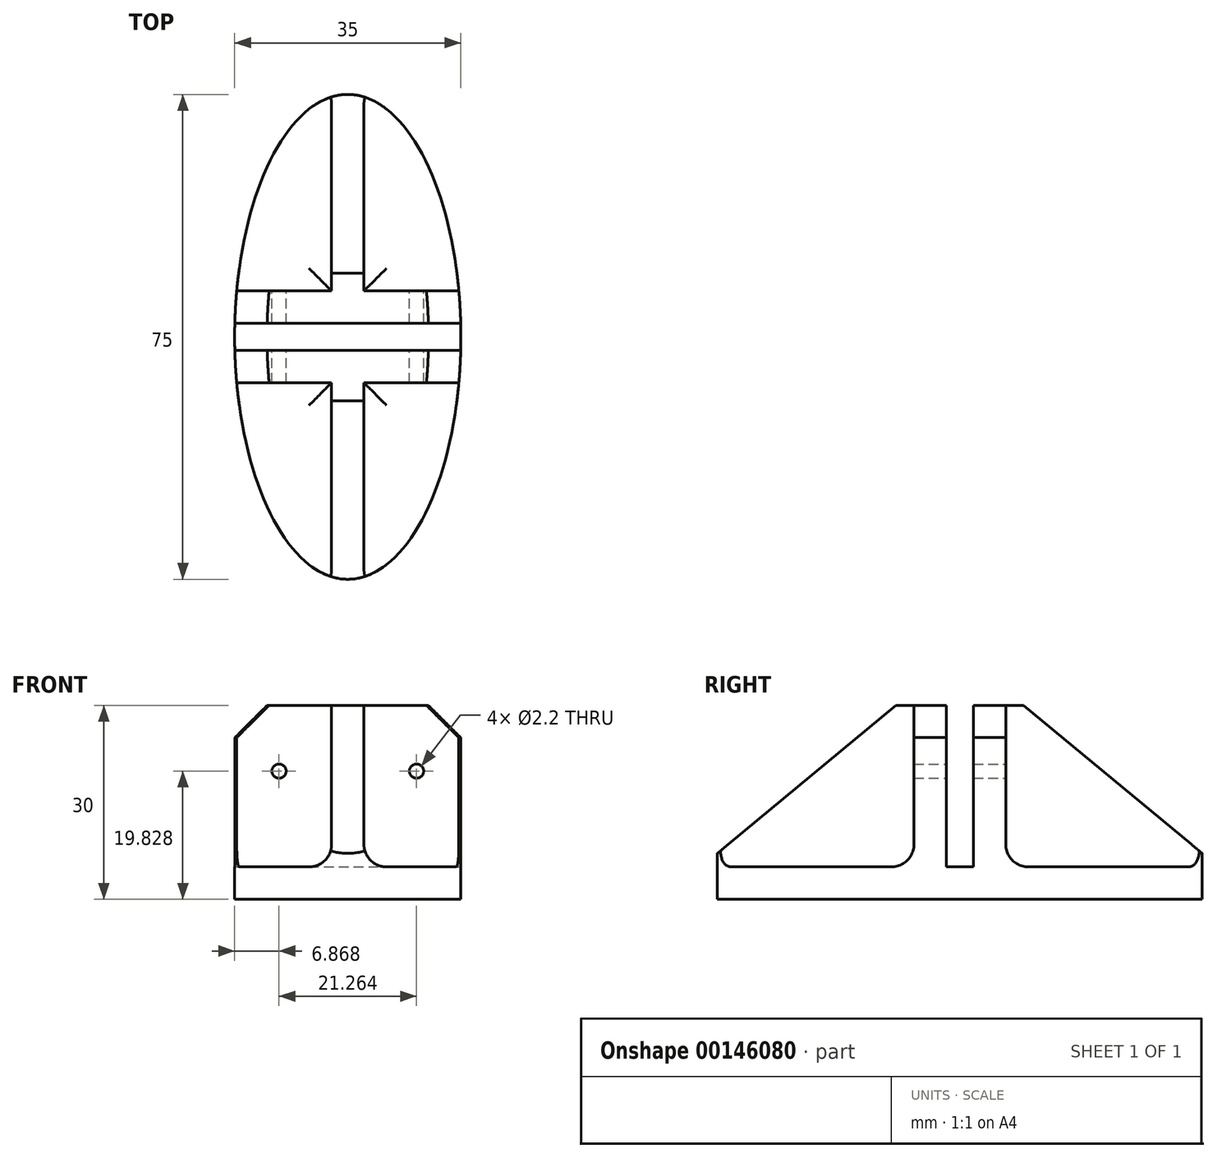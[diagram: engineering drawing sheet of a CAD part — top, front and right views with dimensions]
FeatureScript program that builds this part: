
annotation { "Feature Type Name" : "Feature", "Feature Type Description" : "" }
export const myFeature = defineFeature(function(context is Context, id is Id, definition is map)
    precondition{}
    {
        {
            var Q0;
            Q0=qCreatedBy(makeId("Top.planeOp"),FACE);
            var sketch = newSketch(context, id + "F0", { "sketchPlane" : qUnion([Q0])});
            skEllipse(sketch, "E0", {"center": v(0, 0) * mm, "majorRadius": 37.5 * mm, "minorRadius": 17.5 * mm, "majorAxis": v(0, 1)});
            skSolve(sketch);
        }
        {
            var Q0;
            Q0 = qSketchRegion(id + "F0", true);
            extrude(context, id + "F1", {"entities" : qUnion([Q0]), "depth" : 30 * mm});
        }
        {
            var Q0;
            Q0=makeQuery(id+"F1.opExtrude","CAP_FACE",FACE,{"disambiguationData":[OSD([sQuery(id+"F0.wireOp",EDGE,"E0")])],"isStart":false});
            var sketch = newSketch(context, id + "F2", { "sketchPlane" : qUnion([Q0])});
            skLineSegment(sketch, "E1.bottom", {"start": v(-21.5, 2.1) * mm, "end": v(21.5, 2.1) * mm});
            skLineSegment(sketch, "E1.top", {"start": v(-21.5, -2.1) * mm, "end": v(21.5, -2.1) * mm});
            skLineSegment(sketch, "E1.left", {"start": v(-21.5, 2.1) * mm, "end": v(-21.5, -2.1) * mm});
            skLineSegment(sketch, "E1.right", {"start": v(21.5, 2.1) * mm, "end": v(21.5, -2.1) * mm});
            skPoint(sketch, "E1.middle", {"position": v(0, 0) * mm});
            skSolve(sketch);
        }
        {
            var Q0;
            Q0 = qSketchRegion(id + "F2", true);
            extrude(context, id + "F3", {"entities" : qUnion([Q0]), "operationType" : NewBodyOperationType.REMOVE, "oppositeDirection" : true, "depth" : 25 * mm});
        }
        {
            var Q0;
            {var subQ0=sQuery(id+"F0.wireOp",EDGE,"E0");Q0=makeQuery(id+"F3.boolean.opBoolean","SPLIT",FACE,{"disambiguationData":[TD([makeQuery(id+"F3.opExtrude","SWEPT_FACE",FACE,{"disambiguationData":[OSD([sQuery(id+"F2.wireOp",EDGE,"E1.bottom")])]})])],"derivedFrom":makeQuery(id+"F1.opExtrude","CAP_FACE",FACE,{"disambiguationData":[OSD([subQ0])],"isStart":false})});}
            var sketch = newSketch(context, id + "F4", { "sketchPlane" : qUnion([Q0])});
            skLineSegment(sketch, "E2.bottom", {"start": v(-21.55, 7.1) * mm, "end": v(-2.5, 7.1) * mm});
            skLineSegment(sketch, "E2.top", {"start": v(-21.55, 47.53) * mm, "end": v(-2.5, 47.53) * mm});
            skLineSegment(sketch, "E2.left", {"start": v(-21.55, 7.1) * mm, "end": v(-21.55, 47.53) * mm});
            skLineSegment(sketch, "E2.right", {"start": v(-2.5, 7.1) * mm, "end": v(-2.5, 47.53) * mm});
            skLineSegment(sketch, "E3.MirrorCS", {"start": v(2.5, 7.1) * mm, "end": v(2.5, 47.53) * mm});
            skLineSegment(sketch, "E4.MirrorCS", {"start": v(21.55, 7.1) * mm, "end": v(21.55, 47.53) * mm});
            skLineSegment(sketch, "E5.MirrorCS", {"start": v(21.55, 7.1) * mm, "end": v(2.5, 7.1) * mm});
            skLineSegment(sketch, "E6.MirrorCS", {"start": v(21.55, 47.53) * mm, "end": v(2.5, 47.53) * mm});
            skLineSegment(sketch, "E7.MirrorCS", {"start": v(21.55, -7.1) * mm, "end": v(2.5, -7.1) * mm});
            skLineSegment(sketch, "E8.MirrorCS", {"start": v(21.55, -7.1) * mm, "end": v(21.55, -47.53) * mm});
            skLineSegment(sketch, "E9.MirrorCS", {"start": v(2.5, -7.1) * mm, "end": v(2.5, -47.53) * mm});
            skLineSegment(sketch, "E10.MirrorCS", {"start": v(-2.5, -7.1) * mm, "end": v(-2.5, -47.53) * mm});
            skLineSegment(sketch, "E11.MirrorCS", {"start": v(-21.55, -7.1) * mm, "end": v(-21.55, -47.53) * mm});
            skLineSegment(sketch, "E12.MirrorCS", {"start": v(-21.55, -47.53) * mm, "end": v(-2.5, -47.53) * mm});
            skLineSegment(sketch, "E13.MirrorCS", {"start": v(21.55, -47.53) * mm, "end": v(2.5, -47.53) * mm});
            skLineSegment(sketch, "E14.MirrorCS", {"start": v(-21.55, -7.1) * mm, "end": v(-2.5, -7.1) * mm});
            skSolve(sketch);
        }
        {
            var Q0;
            Q0 = qSketchRegion(id + "F4", true);
            extrude(context, id + "F5", {"entities" : qUnion([Q0]), "operationType" : NewBodyOperationType.REMOVE, "oppositeDirection" : true, "depth" : 25 * mm});
        }
        {
            var Q0;
            Q0=qCreatedBy(makeId("Right.planeOp"),FACE);
            var sketch = newSketch(context, id + "F6", { "sketchPlane" : qUnion([Q0])});
            skLineSegment(sketch, "E15", {"start": v(5.91, 33.28) * mm, "end": v(42.13, 3.27) * mm});
            skLineSegment(sketch, "E16", {"start": v(42.13, 3.27) * mm, "end": v(40.75, 34.27) * mm});
            skLineSegment(sketch, "E17", {"start": v(40.75, 34.27) * mm, "end": v(5.91, 33.28) * mm});
            skLineSegment(sketch, "E18.MirrorCS", {"start": v(-42.13, 3.27) * mm, "end": v(-40.75, 34.27) * mm});
            skLineSegment(sketch, "E19.MirrorCS", {"start": v(-40.75, 34.27) * mm, "end": v(-5.91, 33.28) * mm});
            skLineSegment(sketch, "E20.MirrorCS", {"start": v(-5.91, 33.28) * mm, "end": v(-42.13, 3.27) * mm});
            skSolve(sketch);
        }
        {
            var Q0;
            Q0 = qSketchRegion(id + "F6", true);
            extrude(context, id + "F7", {"entities" : qUnion([Q0]), "operationType" : NewBodyOperationType.REMOVE, "endBound" : BoundingType.SYMMETRIC, "depth" : 25 * mm});
        }
        {
            var Q0;
            Q0=makeQuery(id+"F5.boolean.opBoolean","COPY",FACE,{"derivedFrom":makeQuery(id+"F5.opExtrude","SWEPT_FACE",FACE,{"disambiguationData":[OSD([sQuery(id+"F4.wireOp",EDGE,"E5.MirrorCS")])]})});
            var sketch = newSketch(context, id + "F8", { "sketchPlane" : qUnion([Q0])});
            skPoint(sketch, "E21", {"position": v(-10.63, 19.83) * mm});
            skPoint(sketch, "E22.MirrorP", {"position": v(10.63, 19.83) * mm});
            skSolve(sketch);
        }
        {
            var Q0;
            Q0=sQuery(id+"F8.wireOp",VERTEX,"E21");
            var Q1;
            Q1=sQuery(id+"F8.wireOp",VERTEX,"E22.MirrorP");
            var Q2;
            Q2=makeQuery(id+"F1.opExtrude","SWEPT_BODY",BODY,{"disambiguationData":[OSD([sQuery(id+"F0.wireOp",EDGE,"E0")])]});
            hole(context, id + "F9", {"style" : HoleStyle.SIMPLE, "endStyle" : HoleEndStyle.BLIND, "holeDiameter" : 2.2 * mm, "holeDepth" : 20 * mm, "locations" : qUnion([Q0, Q1]), "scope" : qUnion([Q2])});
        }
        {
            var Q0;
            {var subQ0=sQuery(id+"F0.wireOp",EDGE,"E0");var subQ3=makeQuery(id+"F3.opExtrude","SWEPT_FACE",FACE,{"disambiguationData":[OSD([sQuery(id+"F2.wireOp",EDGE,"E1.bottom")])]});Q0=makeQuery(id+"F5.boolean.opBoolean","SPLIT",EDGE,{"disambiguationData":[TD([makeQuery(id+"F5.opExtrude","SWEPT_FACE",FACE,{"disambiguationData":[OSD([sQuery(id+"F4.wireOp",EDGE,"E5.MirrorCS")])]})])],"derivedFrom":makeQuery(id+"F3.boolean.opBoolean","SPLIT",EDGE,{"disambiguationData":[TD([subQ3])],"derivedFrom":makeQuery(id+"F1.opExtrude","CAP_EDGE",EDGE,{"disambiguationData":[OSD([subQ0])],"isStart":false})})});}
            var Q1;
            {var subQ0=sQuery(id+"F0.wireOp",EDGE,"E0");var subQ3=makeQuery(id+"F3.opExtrude","SWEPT_FACE",FACE,{"disambiguationData":[OSD([sQuery(id+"F2.wireOp",EDGE,"E1.top")])]});Q1=makeQuery(id+"F5.boolean.opBoolean","SPLIT",EDGE,{"disambiguationData":[TD([makeQuery(id+"F5.opExtrude","SWEPT_FACE",FACE,{"disambiguationData":[OSD([sQuery(id+"F4.wireOp",EDGE,"E7.MirrorCS")])]})])],"derivedFrom":makeQuery(id+"F3.boolean.opBoolean","SPLIT",EDGE,{"disambiguationData":[TD([subQ3])],"derivedFrom":makeQuery(id+"F1.opExtrude","CAP_EDGE",EDGE,{"disambiguationData":[OSD([subQ0])],"isStart":false})})});}
            var Q2;
            {var subQ0=sQuery(id+"F0.wireOp",EDGE,"E0");var subQ3=makeQuery(id+"F3.opExtrude","SWEPT_FACE",FACE,{"disambiguationData":[OSD([sQuery(id+"F2.wireOp",EDGE,"E1.bottom")])]});Q2=makeQuery(id+"F5.boolean.opBoolean","SPLIT",EDGE,{"disambiguationData":[TD([makeQuery(id+"F5.opExtrude","SWEPT_FACE",FACE,{"disambiguationData":[OSD([sQuery(id+"F4.wireOp",EDGE,"E2.bottom")])]})])],"derivedFrom":makeQuery(id+"F3.boolean.opBoolean","SPLIT",EDGE,{"disambiguationData":[TD([subQ3])],"derivedFrom":makeQuery(id+"F1.opExtrude","CAP_EDGE",EDGE,{"disambiguationData":[OSD([subQ0])],"isStart":false})})});}
            var Q3;
            {var subQ0=sQuery(id+"F0.wireOp",EDGE,"E0");var subQ3=makeQuery(id+"F3.opExtrude","SWEPT_FACE",FACE,{"disambiguationData":[OSD([sQuery(id+"F2.wireOp",EDGE,"E1.top")])]});Q3=makeQuery(id+"F5.boolean.opBoolean","SPLIT",EDGE,{"disambiguationData":[TD([makeQuery(id+"F5.opExtrude","SWEPT_FACE",FACE,{"disambiguationData":[OSD([sQuery(id+"F4.wireOp",EDGE,"E14.MirrorCS")])]})])],"derivedFrom":makeQuery(id+"F3.boolean.opBoolean","SPLIT",EDGE,{"disambiguationData":[TD([subQ3])],"derivedFrom":makeQuery(id+"F1.opExtrude","CAP_EDGE",EDGE,{"disambiguationData":[OSD([subQ0])],"isStart":false})})});}
            chamfer(context, id + "F10", {"entities" : qUnion([Q0, Q1, Q2, Q3]), "width" : 5 * mm, "tangentPropagation" : true});
        }
        {
            var Q0;
            Q0=makeQuery(id+"F5.boolean.opBoolean","COPY",EDGE,{"derivedFrom":makeQuery(id+"F5.opExtrude","CAP_EDGE",EDGE,{"disambiguationData":[OSD([sQuery(id+"F4.wireOp",EDGE,"E2.bottom")])],"isStart":false})});
            var Q1;
            Q1=makeQuery(id+"F5.boolean.opBoolean","COPY",EDGE,{"derivedFrom":makeQuery(id+"F5.opExtrude","CAP_EDGE",EDGE,{"disambiguationData":[OSD([sQuery(id+"F4.wireOp",EDGE,"E2.right")])],"isStart":false})});
            var Q2;
            Q2=makeQuery(id+"F5.boolean.opBoolean","COPY",EDGE,{"derivedFrom":makeQuery(id+"F5.opExtrude","CAP_EDGE",EDGE,{"disambiguationData":[OSD([sQuery(id+"F4.wireOp",EDGE,"E10.MirrorCS")])],"isStart":false})});
            var Q3;
            Q3=makeQuery(id+"F5.boolean.opBoolean","COPY",EDGE,{"derivedFrom":makeQuery(id+"F5.opExtrude","CAP_EDGE",EDGE,{"disambiguationData":[OSD([sQuery(id+"F4.wireOp",EDGE,"E3.MirrorCS")])],"isStart":false})});
            var Q4;
            Q4=makeQuery(id+"F5.boolean.opBoolean","COPY",EDGE,{"derivedFrom":makeQuery(id+"F5.opExtrude","CAP_EDGE",EDGE,{"disambiguationData":[OSD([sQuery(id+"F4.wireOp",EDGE,"E5.MirrorCS")])],"isStart":false})});
            var Q5;
            Q5=makeQuery(id+"F5.boolean.opBoolean","COPY",EDGE,{"derivedFrom":makeQuery(id+"F5.opExtrude","CAP_EDGE",EDGE,{"disambiguationData":[OSD([sQuery(id+"F4.wireOp",EDGE,"E9.MirrorCS")])],"isStart":false})});
            var Q6;
            Q6=makeQuery(id+"F5.boolean.opBoolean","COPY",EDGE,{"derivedFrom":makeQuery(id+"F5.opExtrude","CAP_EDGE",EDGE,{"disambiguationData":[OSD([sQuery(id+"F4.wireOp",EDGE,"E7.MirrorCS")])],"isStart":false})});
            var Q7;
            Q7=makeQuery(id+"F5.boolean.opBoolean","COPY",EDGE,{"derivedFrom":makeQuery(id+"F5.opExtrude","CAP_EDGE",EDGE,{"disambiguationData":[OSD([sQuery(id+"F4.wireOp",EDGE,"E14.MirrorCS")])],"isStart":false})});
            fillet(context, id + "F11", {"entities" : qUnion([Q0, Q1, Q2, Q3, Q4, Q5, Q6, Q7]), "radius" : 3.5 * mm, "tangentPropagation" : true, "allowEdgeOverflow" : false});
        }
    });
